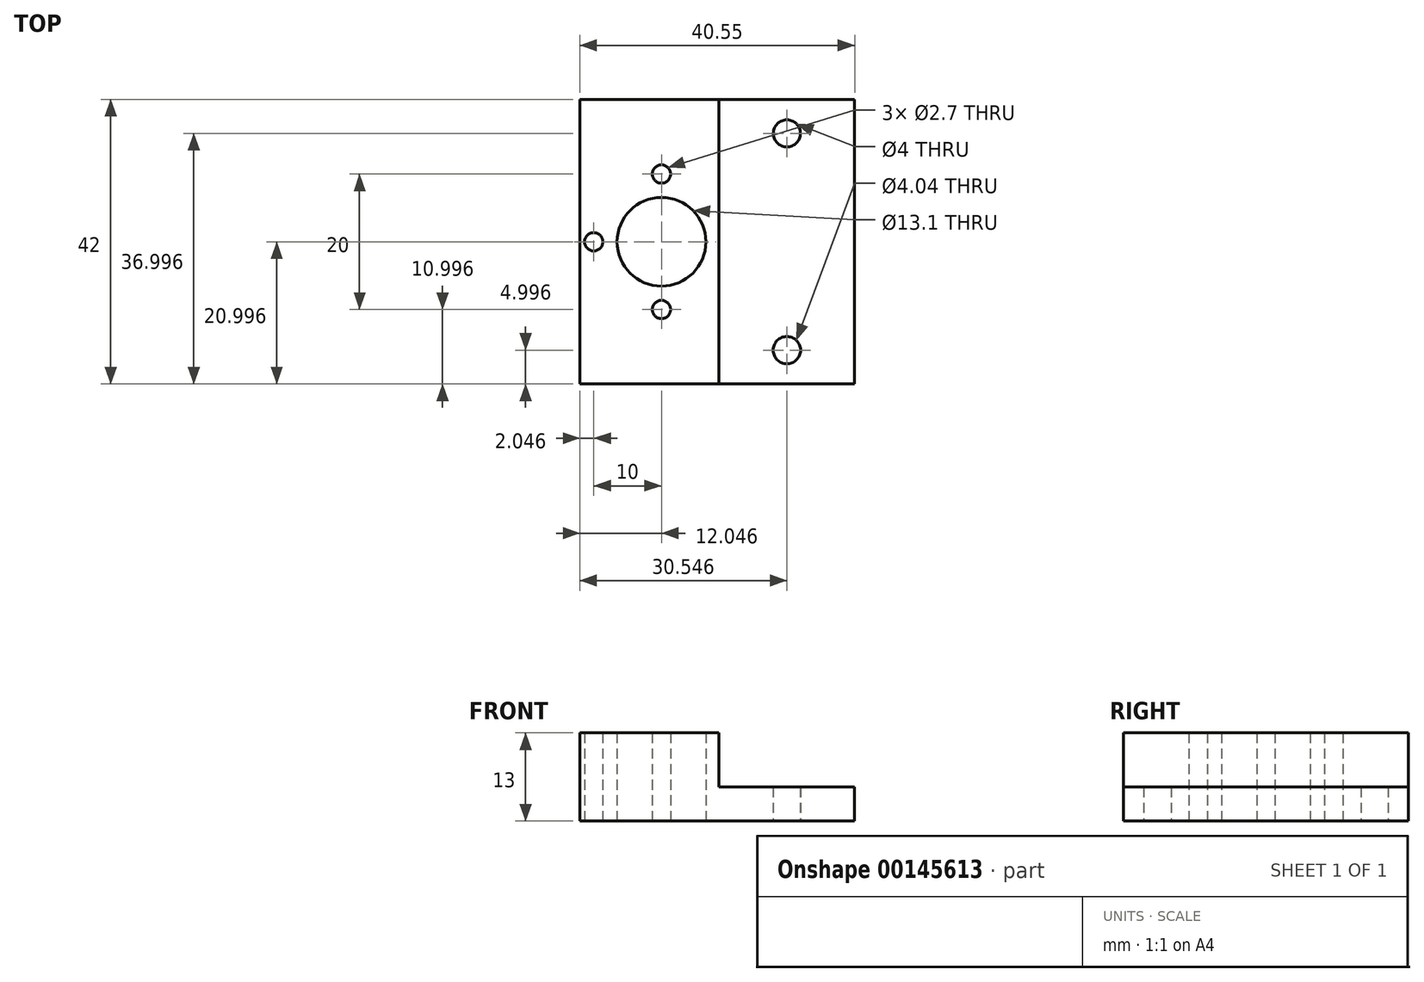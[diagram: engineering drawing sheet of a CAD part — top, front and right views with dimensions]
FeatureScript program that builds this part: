
annotation { "Feature Type Name" : "Feature", "Feature Type Description" : "" }
export const myFeature = defineFeature(function(context is Context, id is Id, definition is map)
    precondition{}
    {
        {
            var Q0;
            Q0=qCreatedBy(makeId("Top.planeOp"),FACE);
            var sketch = newSketch(context, id + "F0", { "sketchPlane" : qUnion([Q0])});
            skLineSegment(sketch, "E0.bottom", {"start": v(-17, 35.17) * mm, "end": v(23.56, 35.17) * mm});
            skLineSegment(sketch, "E0.top", {"start": v(-17, -6.83) * mm, "end": v(23.56, -6.83) * mm});
            skLineSegment(sketch, "E0.left", {"start": v(-17, 35.17) * mm, "end": v(-17, -6.83) * mm});
            skLineSegment(sketch, "E0.right", {"start": v(23.56, 35.17) * mm, "end": v(23.56, -6.83) * mm});
            skLineSegment(sketch, "E1", {"start": v(13.56, 35.17) * mm, "end": v(13.56, -6.83) * mm, "construction": true});
            skLineSegment(sketch, "E2", {"start": v(-17, 14.17) * mm, "end": v(23.56, 14.17) * mm, "construction": true});
            skLineSegment(sketch, "E3", {"start": v(-4.94, 35.17) * mm, "end": v(-4.94, -6.83) * mm, "construction": true});
            skPoint(sketch, "E4", {"position": v(-4.94, 14.17) * mm});
            skCircle(sketch, "E5", {"center": v(13.56, 30.17) * mm, "radius": 2 * mm});
            skCircle(sketch, "E6", {"center": v(13.56, -1.83) * mm, "radius": 2.02 * mm});
            skCircle(sketch, "E7", {"center": v(-4.94, 14.17) * mm, "radius": 6.55 * mm});
            skLineSegment(sketch, "E8", {"start": v(3.56, 35.17) * mm, "end": v(3.56, -6.83) * mm});
            skCircle(sketch, "E9", {"center": v(-4.94, 24.17) * mm, "radius": 1.35 * mm});
            skCircle(sketch, "E10", {"center": v(-4.94, 4.17) * mm, "radius": 1.35 * mm});
            skCircle(sketch, "E11", {"center": v(-14.94, 14.17) * mm, "radius": 1.35 * mm});
            skSolve(sketch);
        }
        {
            var Q0;
            {var subQ0=sQuery(id+"F0.wireOp",EDGE,"E0.right");Q0=makeQuery(id+"F0.imprint","IMPRINT",FACE,{"disambiguationData":[TD([[makeQuery(id+"F0.imprint","IMPRINT",EDGE,{"derivedFrom":subQ0}),-1.0]])]});}
            extrude(context, id + "F1", {"entities" : qUnion([Q0]), "offsetDistance" : 25 * mm, "depth" : 5 * mm});
        }
        {
            var Q0;
            {var subQ0=sQuery(id+"F0.wireOp",EDGE,"E0.left");Q0=makeQuery(id+"F0.imprint","IMPRINT",FACE,{"disambiguationData":[TD([[makeQuery(id+"F0.imprint","IMPRINT",EDGE,{"derivedFrom":subQ0}),1.0]])]});}
            extrude(context, id + "F2", {"entities" : qUnion([Q0]), "operationType" : NewBodyOperationType.ADD, "offsetDistance" : 25 * mm, "depth" : (8 + 5) * mm});
        }
    });
